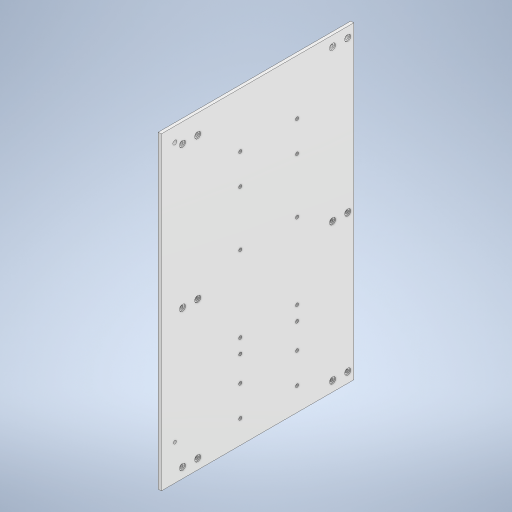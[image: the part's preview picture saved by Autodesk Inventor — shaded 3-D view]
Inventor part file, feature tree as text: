
AUTODESK INVENTOR PART (.ipt)
format: ipt  version: 2024.3 (Build 283343000, 343)  size: 473,600 bytes
history: native  units: mm
features: extrude x17, sketch x17, other x1, projected_geometry x1
ambient origin geometry x8: Origin, YZ Plane, XZ Plane, XY Plane, X Axis, Y Axis, Z Axis, Center Point
bodies: Body1 (feature_tree)
feature tree (36):
  other  "ソリッド1"
  extrude  "押し出し1"  Depth=150.0mm
  extrude  "押し出し2"  Depth=175.0mm
  sketch  "スケッチ3"
  extrude  "押し出し4"  Depth=3.0mm TaperAngle=0.0deg
  extrude  "押し出し5"  Depth=3.0mm
  extrude  "押し出し7"  Depth=6.0mm
  extrude  "押し出し8"  Depth=15.0mm
  extrude  "押し出し9"  Depth=3.0mm
  extrude  "押し出し10"  TaperAngle=0.0deg  [1 undecoded]
  extrude  "押し出し11"  Depth=6.0mm
  extrude  "押し出し12"  Depth=3.0mm
  extrude  "押し出し13"  Depth=15.0mm
  extrude  "押し出し14"  Depth=3.0mm
  extrude  "押し出し15"  Depth=3.0mm
  extrude  "押し出し16"  Depth=3.0mm
  extrude  "押し出し17"  Depth=6.0mm
  extrude  "押し出し18"  Depth=15.0mm
  extrude  "押し出し19"  Depth=5.0mm
  sketch  "スケッチ1"
  sketch  "スケッチ2"
  sketch  "スケッチ6"
  sketch  "スケッチ7"
  sketch  "スケッチ9"
  sketch  "スケッチ10"
  sketch  "スケッチ11"
  sketch  "スケッチ12"
  sketch  "スケッチ13"
  sketch  "スケッチ14"
  sketch  "スケッチ15"
  sketch  "スケッチ16"
  sketch  "スケッチ17"
  sketch  "スケッチ18"
  sketch  "スケッチ19"
  sketch  "スケッチ20"
  projected_geometry  "投影ループ1"
note: 1 required parameter value undecoded (feature->parameter linkage not recoverable at this tier; creation-order binding heuristic only, values carry confidence <= 0.55)
